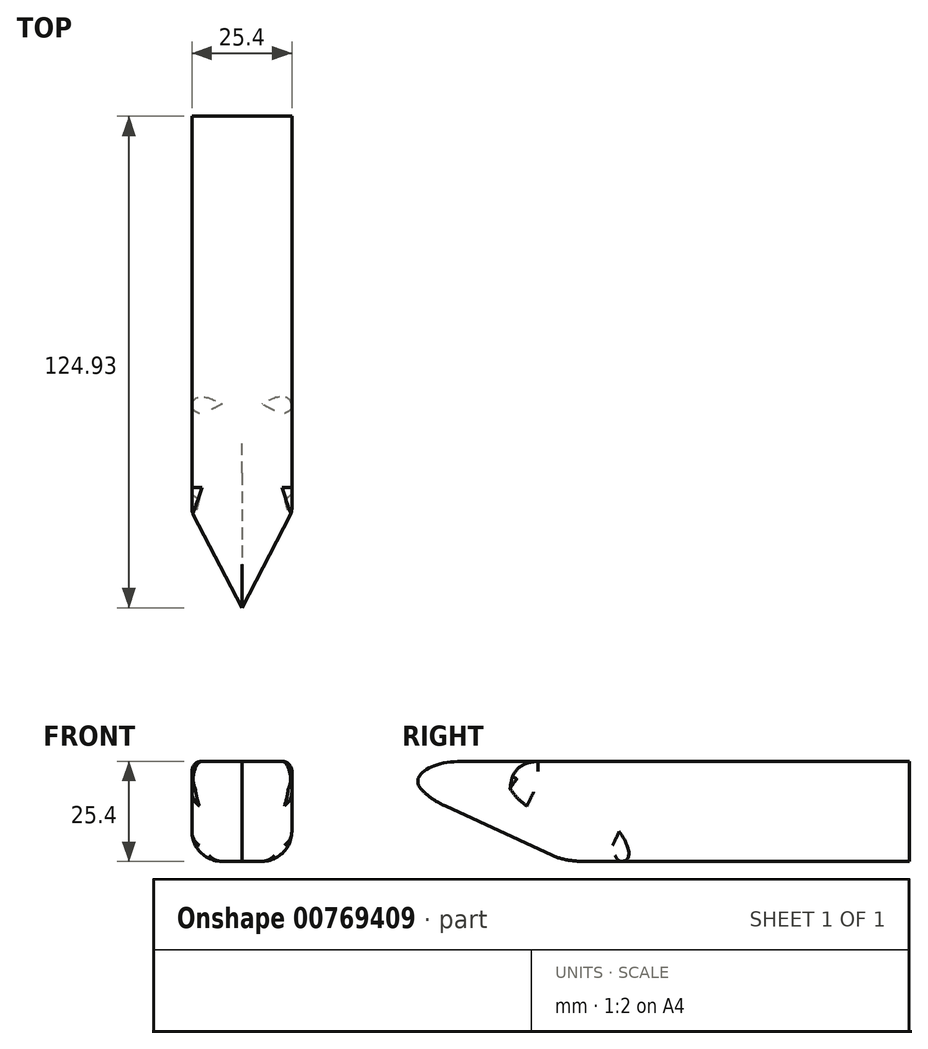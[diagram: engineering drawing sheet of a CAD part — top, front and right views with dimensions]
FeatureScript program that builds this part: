
annotation { "Feature Type Name" : "Feature", "Feature Type Description" : "" }
export const myFeature = defineFeature(function(context is Context, id is Id, definition is map)
    precondition{}
    {
        {
            var Q0;
            Q0=qCreatedBy(makeId("Top.planeOp"),FACE);
            var sketch = newSketch(context, id + "F0", { "sketchPlane" : qUnion([Q0])});
            skLineSegment(sketch, "E0.bottom", {"start": v(-12.7, 49.05) * mm, "end": v(12.7, 49.05) * mm});
            skLineSegment(sketch, "E0.top", {"start": v(-12.7, -52.55) * mm, "end": v(12.7, -52.55) * mm});
            skLineSegment(sketch, "E0.left", {"start": v(-12.7, 49.05) * mm, "end": v(-12.7, -52.55) * mm});
            skLineSegment(sketch, "E0.right", {"start": v(12.7, 49.05) * mm, "end": v(12.7, -52.55) * mm});
            skPoint(sketch, "E0.middle", {"position": v(0, -1.75) * mm});
            skLineSegment(sketch, "E1", {"start": v(-12.7, -52.55) * mm, "end": v(0, -76.97) * mm});
            skLineSegment(sketch, "E2", {"start": v(12.7, -52.55) * mm, "end": v(0, -76.97) * mm});
            skSolve(sketch);
        }
        {
            var Q0;
            Q0=makeQuery(id+"F0.imprint","IMPRINT",FACE,{"disambiguationData":[TD([[makeQuery(id+"F0.imprint","IMPRINT",EDGE,{"derivedFrom":sQuery(id+"F0.wireOp",EDGE,"E0.bottom")}),-1.0]])]});
            var Q1;
            Q1=makeQuery(id+"F0.imprint","IMPRINT",FACE,{"disambiguationData":[TD([[makeQuery(id+"F0.imprint","IMPRINT",EDGE,{"derivedFrom":sQuery(id+"F0.wireOp",EDGE,"E0.top")}),-1.0]])]});
            extrude(context, id + "F1", {"entities" : qUnion([Q0, Q1]), "depth" : 25.4 * mm, "offsetDistance" : 25.4 * mm});
        }
        {
            var Q0;
            Q0=makeQuery(id+"F1.opExtrude","CAP_EDGE",EDGE,{"disambiguationData":[OSD([sQuery(id+"F0.wireOp",EDGE,"E2")])],"isStart":true});
            var Q1;
            Q1=makeQuery(id+"F1.opExtrude","CAP_EDGE",EDGE,{"disambiguationData":[OSD([sQuery(id+"F0.wireOp",EDGE,"E1")])],"isStart":true});
            chamfer(context, id + "F2", {"entities" : qUnion([Q0, Q1]), "width" : 17.78 * mm, "tangentPropagation" : true});
        }
        {
            var Q0;
            {var subQ0=sQuery(id+"F0.wireOp",EDGE,"E2");Q0=makeQuery(id+"F2.opChamfer","BLEND_EDGE",EDGE,{"blendedFrom":[makeQuery(id+"F1.opExtrude","CAP_EDGE",EDGE,{"disambiguationData":[OSD([subQ0])],"isStart":true}),makeQuery(id+"F1.opExtrude","SWEPT_FACE",FACE,{"disambiguationData":[OSD([subQ0])]})],"blendedInto":[makeQuery(id+"F1.opExtrude","SWEPT_FACE",FACE,{"disambiguationData":[OSD([subQ0])]})]});}
            var Q1;
            {var subQ0=sQuery(id+"F0.wireOp",EDGE,"E1");Q1=makeQuery(id+"F2.opChamfer","BLEND_EDGE",EDGE,{"blendedFrom":[makeQuery(id+"F1.opExtrude","CAP_EDGE",EDGE,{"disambiguationData":[OSD([subQ0])],"isStart":true}),makeQuery(id+"F1.opExtrude","SWEPT_FACE",FACE,{"disambiguationData":[OSD([subQ0])]})],"blendedInto":[makeQuery(id+"F1.opExtrude","SWEPT_FACE",FACE,{"disambiguationData":[OSD([subQ0])]})]});}
            fillet(context, id + "F3", {"entities" : qUnion([Q0, Q1]), "radius" : 12.7 * mm, "tangentPropagation" : true, "allowEdgeOverflow" : false});
        }
        {
            var Q0;
            Q0=makeQuery(id+"F1.opExtrude","CAP_EDGE",EDGE,{"disambiguationData":[OSD([sQuery(id+"F0.wireOp",EDGE,"E0.right")])],"isStart":true});
            var Q1;
            Q1=makeQuery(id+"F1.opExtrude","CAP_EDGE",EDGE,{"disambiguationData":[OSD([sQuery(id+"F0.wireOp",EDGE,"E0.left")])],"isStart":true});
            fillet(context, id + "F4", {"entities" : qUnion([Q0, Q1]), "radius" : 7.62 * mm, "tangentPropagation" : true, "allowEdgeOverflow" : false});
        }
        {
            var Q0;
            Q0=makeQuery(id+"F1.opExtrude","CAP_EDGE",EDGE,{"disambiguationData":[OSD([sQuery(id+"F0.wireOp",EDGE,"E2")])],"isStart":false});
            var Q1;
            Q1=makeQuery(id+"F2.opChamfer","BLEND_EDGE",EDGE,{"blendedFrom":[makeQuery(id+"F1.opExtrude","CAP_EDGE",EDGE,{"disambiguationData":[OSD([sQuery(id+"F0.wireOp",EDGE,"E2")])],"isStart":true}),makeQuery(id+"F1.opExtrude","SWEPT_FACE",FACE,{"disambiguationData":[OSD([sQuery(id+"F0.wireOp",EDGE,"E0.right")])]})],"blendedInto":[makeQuery(id+"F1.opExtrude","SWEPT_FACE",FACE,{"disambiguationData":[OSD([sQuery(id+"F0.wireOp",EDGE,"E0.right")])]})]});
            var Q2;
            {var subQ0=sQuery(id+"F0.wireOp",EDGE,"E2");Q2=makeQuery(id+"F3.opFillet","BLEND_EDGE",EDGE,{"blendedFrom":[makeQuery(id+"F2.opChamfer","BLEND_EDGE",EDGE,{"blendedFrom":[makeQuery(id+"F1.opExtrude","CAP_EDGE",EDGE,{"disambiguationData":[OSD([subQ0])],"isStart":true}),makeQuery(id+"F1.opExtrude","SWEPT_FACE",FACE,{"disambiguationData":[OSD([subQ0])]})],"blendedInto":[makeQuery(id+"F1.opExtrude","SWEPT_FACE",FACE,{"disambiguationData":[OSD([subQ0])]})]}),makeQuery(id+"F1.opExtrude","SWEPT_FACE",FACE,{"disambiguationData":[OSD([sQuery(id+"F0.wireOp",EDGE,"E0.right")])]})],"blendedInto":[makeQuery(id+"F1.opExtrude","SWEPT_FACE",FACE,{"disambiguationData":[OSD([sQuery(id+"F0.wireOp",EDGE,"E0.right")])]})]});}
            var Q3;
            Q3=makeQuery(id+"F1.opExtrude","SWEPT_EDGE",EDGE,{"disambiguationData":[OSD([sQuery(id+"F0.wireOp",EDGE,"E0.top"),sQuery(id+"F0.wireOp",EDGE,"E0.right"),sQuery(id+"F0.wireOp",EDGE,"E2")])]});
            var Q4;
            Q4=makeQuery(id+"F4.opFillet","BLEND_EDGE",EDGE,{"blendedFrom":[makeQuery(id+"F1.opExtrude","CAP_EDGE",EDGE,{"disambiguationData":[OSD([sQuery(id+"F0.wireOp",EDGE,"E0.right")])],"isStart":true}),makeQuery(id+"F2.opChamfer","BLEND_FACE",FACE,{"disambiguationData":[OSD([sQuery(id+"F0.wireOp",EDGE,"E2")])]})],"blendedInto":[makeQuery(id+"F2.opChamfer","BLEND_FACE",FACE,{"disambiguationData":[OSD([sQuery(id+"F0.wireOp",EDGE,"E2")])]})]});
            var Q5;
            Q5=makeQuery(id+"F2.opChamfer","BLEND_EDGE",EDGE,{"blendedFrom":[makeQuery(id+"F1.opExtrude","CAP_EDGE",EDGE,{"disambiguationData":[OSD([sQuery(id+"F0.wireOp",EDGE,"E1")])],"isStart":true}),makeQuery(id+"F1.opExtrude","SWEPT_FACE",FACE,{"disambiguationData":[OSD([sQuery(id+"F0.wireOp",EDGE,"E0.left")])]})],"blendedInto":[makeQuery(id+"F1.opExtrude","SWEPT_FACE",FACE,{"disambiguationData":[OSD([sQuery(id+"F0.wireOp",EDGE,"E0.left")])]})]});
            var Q6;
            {var subQ0=sQuery(id+"F0.wireOp",EDGE,"E1");Q6=makeQuery(id+"F3.opFillet","BLEND_EDGE",EDGE,{"blendedFrom":[makeQuery(id+"F2.opChamfer","BLEND_EDGE",EDGE,{"blendedFrom":[makeQuery(id+"F1.opExtrude","CAP_EDGE",EDGE,{"disambiguationData":[OSD([subQ0])],"isStart":true}),makeQuery(id+"F1.opExtrude","SWEPT_FACE",FACE,{"disambiguationData":[OSD([subQ0])]})],"blendedInto":[makeQuery(id+"F1.opExtrude","SWEPT_FACE",FACE,{"disambiguationData":[OSD([subQ0])]})]}),makeQuery(id+"F1.opExtrude","SWEPT_FACE",FACE,{"disambiguationData":[OSD([sQuery(id+"F0.wireOp",EDGE,"E0.left")])]})],"blendedInto":[makeQuery(id+"F1.opExtrude","SWEPT_FACE",FACE,{"disambiguationData":[OSD([sQuery(id+"F0.wireOp",EDGE,"E0.left")])]})]});}
            var Q7;
            Q7=makeQuery(id+"F1.opExtrude","CAP_EDGE",EDGE,{"disambiguationData":[OSD([sQuery(id+"F0.wireOp",EDGE,"E1")])],"isStart":false});
            var Q8;
            Q8=makeQuery(id+"F1.opExtrude","SWEPT_EDGE",EDGE,{"disambiguationData":[OSD([sQuery(id+"F0.wireOp",EDGE,"E0.top"),sQuery(id+"F0.wireOp",EDGE,"E0.left"),sQuery(id+"F0.wireOp",EDGE,"E1")])]});
            var Q9;
            Q9=makeQuery(id+"F4.opFillet","BLEND_EDGE",EDGE,{"blendedFrom":[makeQuery(id+"F1.opExtrude","CAP_EDGE",EDGE,{"disambiguationData":[OSD([sQuery(id+"F0.wireOp",EDGE,"E0.left")])],"isStart":true}),makeQuery(id+"F2.opChamfer","BLEND_FACE",FACE,{"disambiguationData":[OSD([sQuery(id+"F0.wireOp",EDGE,"E1")])]})],"blendedInto":[makeQuery(id+"F2.opChamfer","BLEND_FACE",FACE,{"disambiguationData":[OSD([sQuery(id+"F0.wireOp",EDGE,"E1")])]})]});
            fillet(context, id + "F5", {"entities" : qUnion([Q0, Q1, Q2, Q3, Q4, Q5, Q6, Q7, Q8, Q9]), "radius" : 5.08 * mm, "tangentPropagation" : true, "allowEdgeOverflow" : false});
        }
        {
            var Q0;
            Q0=makeQuery(id+"F1.opExtrude","CAP_EDGE",EDGE,{"disambiguationData":[OSD([sQuery(id+"F0.wireOp",EDGE,"E0.right")])],"isStart":false});
            var Q1;
            Q1=makeQuery(id+"F1.opExtrude","CAP_EDGE",EDGE,{"disambiguationData":[OSD([sQuery(id+"F0.wireOp",EDGE,"E0.left")])],"isStart":false});
            fillet(context, id + "F6", {"entities" : qUnion([Q0, Q1]), "radius" : 2.54 * mm, "tangentPropagation" : true, "allowEdgeOverflow" : false});
        }
    });
